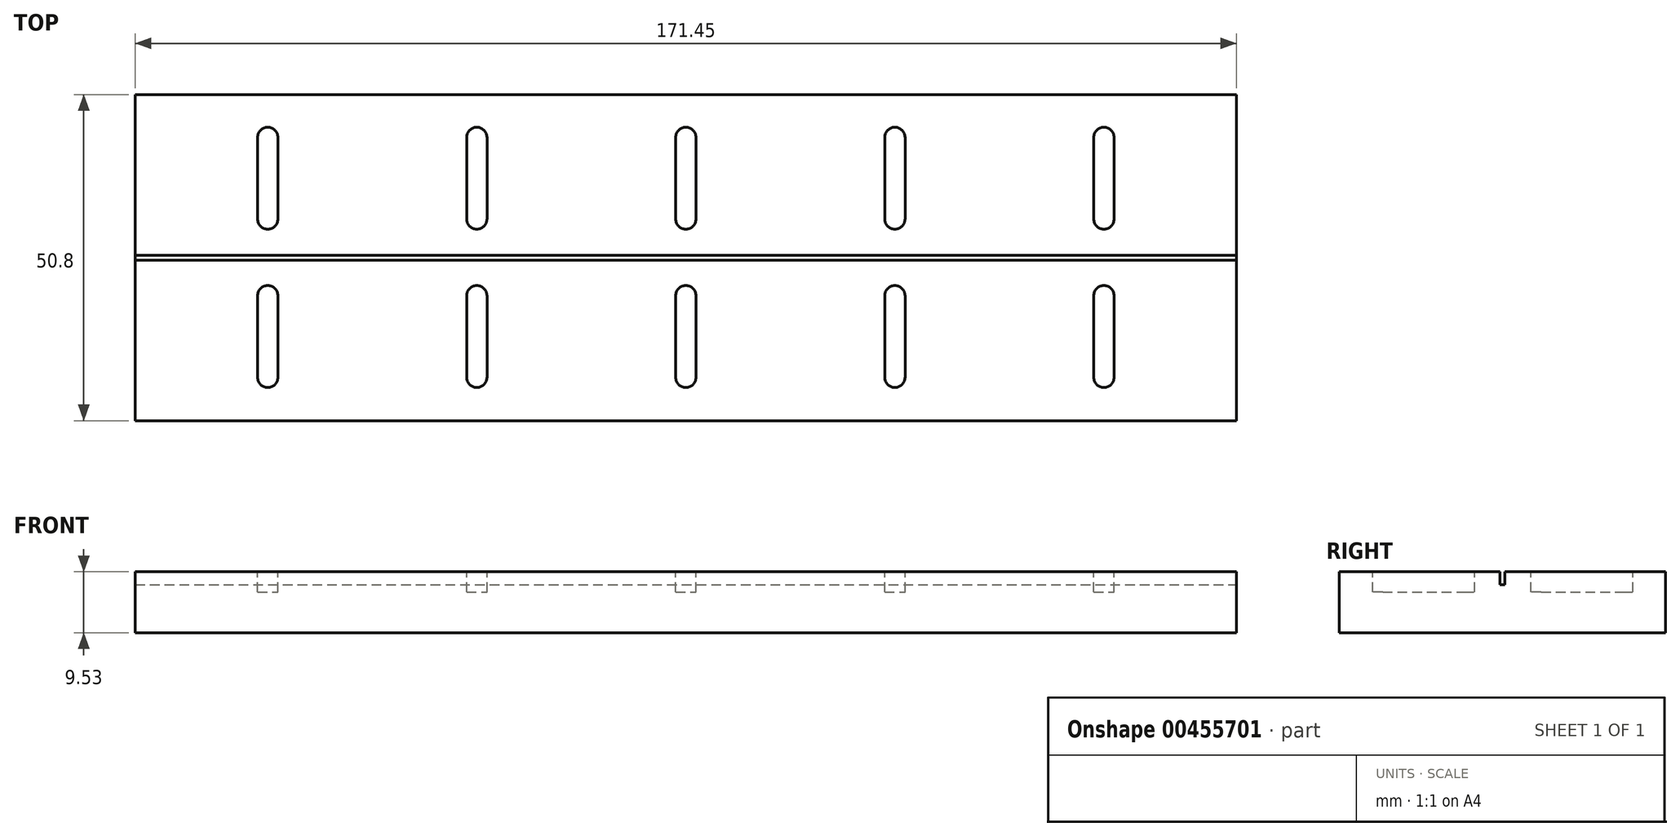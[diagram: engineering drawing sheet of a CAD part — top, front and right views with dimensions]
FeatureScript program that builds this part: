
annotation { "Feature Type Name" : "Feature", "Feature Type Description" : "" }
export const myFeature = defineFeature(function(context is Context, id is Id, definition is map)
    precondition{}
    {
        {
            var Q0;
            Q0=qCreatedBy(makeId("Top.planeOp"),FACE);
            var sketch = newSketch(context, id + "F0", { "sketchPlane" : qUnion([Q0])});
            skLineSegment(sketch, "E0.bottom", {"start": v(112.18, 25.34) * mm, "end": v(-40.22, 25.34) * mm});
            skLineSegment(sketch, "E0.top", {"start": v(112.18, -25.46) * mm, "end": v(-40.22, -25.46) * mm});
            skLineSegment(sketch, "E0.left", {"start": v(112.18, 25.34) * mm, "end": v(112.18, -25.46) * mm});
            skLineSegment(sketch, "E0.right", {"start": v(-40.22, 25.34) * mm, "end": v(-40.22, -25.46) * mm});
            skPoint(sketch, "E0.middle", {"position": v(35.98, -0.06) * mm});
            skLineSegment(sketch, "E1.bottom", {"start": v(-40.22, 0.32) * mm, "end": v(112.18, 0.32) * mm});
            skLineSegment(sketch, "E1.top", {"start": v(-40.22, -0.44) * mm, "end": v(112.18, -0.44) * mm});
            skLineSegment(sketch, "E1.left", {"start": v(-40.22, 0.32) * mm, "end": v(-40.22, -0.44) * mm});
            skLineSegment(sketch, "E1.right", {"start": v(112.18, 0.32) * mm, "end": v(112.18, -0.44) * mm});
            skSolve(sketch);
        }
        {
            var Q0;
            {var subQ0=sQuery(id+"F0.wireOp",EDGE,"E0.top");Q0=makeQuery(id+"F0.imprint","IMPRINT",FACE,{"disambiguationData":[TD([[makeQuery(id+"F0.imprint","IMPRINT",EDGE,{"derivedFrom":subQ0}),-1.0]])]});}
            var Q1;
            {var subQ0=sQuery(id+"F0.wireOp",EDGE,"E0.bottom");Q1=makeQuery(id+"F0.imprint","IMPRINT",FACE,{"disambiguationData":[TD([[makeQuery(id+"F0.imprint","IMPRINT",EDGE,{"derivedFrom":subQ0}),1.0]])]});}
            var Q2;
            Q2=makeQuery(id+"F0.imprint","IMPRINT",FACE,{"disambiguationData":[TD([[makeQuery(id+"F0.imprint","IMPRINT",EDGE,{"derivedFrom":sQuery(id+"F0.wireOp",EDGE,"E1.bottom")}),-1.0]])]});
            extrude(context, id + "F1", {"entities" : qUnion([Q0, Q1, Q2]), "oppositeDirection" : true, "depth" : 9.52 * mm});
        }
        {
            var Q0;
            Q0=makeQuery(id+"F0.imprint","IMPRINT",FACE,{"disambiguationData":[TD([[makeQuery(id+"F0.imprint","IMPRINT",EDGE,{"derivedFrom":sQuery(id+"F0.wireOp",EDGE,"E1.bottom")}),-1.0]])]});
            extrude(context, id + "F2", {"entities" : qUnion([Q0]), "operationType" : NewBodyOperationType.REMOVE, "oppositeDirection" : true, "depth" : 2.03 * mm});
        }
        {
            var Q0;
            {var subQ0=sQuery(id+"F0.wireOp",EDGE,"E0.bottom");var subQ1=sQuery(id+"F0.wireOp",EDGE,"E1.left");var subQ2=sQuery(id+"F0.wireOp",EDGE,"E0.right");var subQ3=sQuery(id+"F0.wireOp",EDGE,"E1.right");var subQ4=sQuery(id+"F0.wireOp",EDGE,"E0.left");Q0=makeQuery(id+"F2.boolean.opBoolean","SPLIT",FACE,{"disambiguationData":[TD([makeQuery(id+"F1.opExtrude","SWEPT_FACE",FACE,{"disambiguationData":[OSD([subQ0])]})])],"derivedFrom":makeQuery(id+"F1.opExtrude","CAP_FACE",FACE,{"disambiguationData":[OSD([subQ0,sQuery(id+"F0.wireOp",EDGE,"E0.top"),subQ4,subQ2,subQ1,subQ3])],"isStart":true})});}
            var sketch = newSketch(context, id + "F3", { "sketchPlane" : qUnion([Q0])});
            skLineSegment(sketch, "E2.left", {"start": v(-30.7, 5.97) * mm, "end": v(-30.7, 18.67) * mm});
            skLineSegment(sketch, "E2.right", {"start": v(-27.52, 5.97) * mm, "end": v(-27.52, 18.67) * mm});
            skArc(sketch, "E3", {"start": v(-27.52, 18.67) * mm, "mid": v(-29.11, 20.26) * mm, "end": v(-30.7, 18.67) * mm});
            skArc(sketch, "E4", {"start": v(-30.7, 5.97) * mm, "mid": v(-29.11, 4.38) * mm, "end": v(-27.52, 5.97) * mm});
            skArc(sketch, "E5.0.1.0", {"start": v(-30.7, -18.7) * mm, "mid": v(-29.11, -20.28) * mm, "end": v(-27.52, -18.7) * mm});
            skArc(sketch, "E5.0.1.1", {"start": v(-27.52, -6) * mm, "mid": v(-29.11, -4.4) * mm, "end": v(-30.7, -6) * mm});
            skLineSegment(sketch, "E5.0.1.2", {"start": v(-27.52, -18.7) * mm, "end": v(-27.52, -6) * mm});
            skLineSegment(sketch, "E5.0.1.3", {"start": v(-30.7, -18.7) * mm, "end": v(-30.7, -6) * mm});
            skArc(sketch, "E5.1.0.0", {"start": v(1.84, 5.97) * mm, "mid": v(3.43, 4.38) * mm, "end": v(5.02, 5.97) * mm});
            skArc(sketch, "E5.1.0.1", {"start": v(5.02, 18.67) * mm, "mid": v(3.43, 20.26) * mm, "end": v(1.84, 18.67) * mm});
            skLineSegment(sketch, "E5.1.0.2", {"start": v(5.02, 5.97) * mm, "end": v(5.02, 18.67) * mm});
            skLineSegment(sketch, "E5.1.0.3", {"start": v(1.84, 5.97) * mm, "end": v(1.84, 18.67) * mm});
            skArc(sketch, "E5.1.1.0", {"start": v(1.84, -18.7) * mm, "mid": v(3.43, -20.28) * mm, "end": v(5.02, -18.7) * mm});
            skArc(sketch, "E5.1.1.1", {"start": v(5.02, -6) * mm, "mid": v(3.43, -4.4) * mm, "end": v(1.84, -6) * mm});
            skLineSegment(sketch, "E5.1.1.2", {"start": v(5.02, -18.7) * mm, "end": v(5.02, -6) * mm});
            skLineSegment(sketch, "E5.1.1.3", {"start": v(1.84, -18.7) * mm, "end": v(1.84, -6) * mm});
            skArc(sketch, "E5.2.0.0", {"start": v(34.39, 5.97) * mm, "mid": v(35.98, 4.38) * mm, "end": v(37.56, 5.97) * mm});
            skArc(sketch, "E5.2.0.1", {"start": v(37.56, 18.67) * mm, "mid": v(35.98, 20.26) * mm, "end": v(34.39, 18.67) * mm});
            skLineSegment(sketch, "E5.2.0.2", {"start": v(37.56, 5.97) * mm, "end": v(37.56, 18.67) * mm});
            skLineSegment(sketch, "E5.2.0.3", {"start": v(34.39, 5.97) * mm, "end": v(34.39, 18.67) * mm});
            skArc(sketch, "E5.2.1.0", {"start": v(34.39, -18.7) * mm, "mid": v(35.98, -20.28) * mm, "end": v(37.56, -18.7) * mm});
            skArc(sketch, "E5.2.1.1", {"start": v(37.56, -6) * mm, "mid": v(35.98, -4.4) * mm, "end": v(34.39, -6) * mm});
            skLineSegment(sketch, "E5.2.1.2", {"start": v(37.56, -18.7) * mm, "end": v(37.56, -6) * mm});
            skLineSegment(sketch, "E5.2.1.3", {"start": v(34.39, -18.7) * mm, "end": v(34.39, -6) * mm});
            skArc(sketch, "E5.3.0.0", {"start": v(66.93, 5.97) * mm, "mid": v(68.52, 4.38) * mm, "end": v(70.1, 5.97) * mm});
            skArc(sketch, "E5.3.0.1", {"start": v(70.1, 18.67) * mm, "mid": v(68.52, 20.26) * mm, "end": v(66.93, 18.67) * mm});
            skLineSegment(sketch, "E5.3.0.2", {"start": v(70.1, 5.97) * mm, "end": v(70.1, 18.67) * mm});
            skLineSegment(sketch, "E5.3.0.3", {"start": v(66.93, 5.97) * mm, "end": v(66.93, 18.67) * mm});
            skArc(sketch, "E5.3.1.0", {"start": v(66.93, -18.7) * mm, "mid": v(68.52, -20.28) * mm, "end": v(70.1, -18.7) * mm});
            skArc(sketch, "E5.3.1.1", {"start": v(70.1, -6) * mm, "mid": v(68.52, -4.4) * mm, "end": v(66.93, -6) * mm});
            skLineSegment(sketch, "E5.3.1.2", {"start": v(70.1, -18.7) * mm, "end": v(70.1, -6) * mm});
            skLineSegment(sketch, "E5.3.1.3", {"start": v(66.93, -18.7) * mm, "end": v(66.93, -6) * mm});
            skArc(sketch, "E5.4.0.0", {"start": v(99.48, 5.97) * mm, "mid": v(101.06, 4.38) * mm, "end": v(102.65, 5.97) * mm});
            skArc(sketch, "E5.4.0.1", {"start": v(102.65, 18.67) * mm, "mid": v(101.06, 20.26) * mm, "end": v(99.48, 18.67) * mm});
            skLineSegment(sketch, "E5.4.0.2", {"start": v(102.65, 5.97) * mm, "end": v(102.65, 18.67) * mm});
            skLineSegment(sketch, "E5.4.0.3", {"start": v(99.48, 5.97) * mm, "end": v(99.48, 18.67) * mm});
            skArc(sketch, "E5.4.1.0", {"start": v(99.48, -18.7) * mm, "mid": v(101.06, -20.28) * mm, "end": v(102.65, -18.7) * mm});
            skArc(sketch, "E5.4.1.1", {"start": v(102.65, -6) * mm, "mid": v(101.06, -4.4) * mm, "end": v(99.48, -6) * mm});
            skLineSegment(sketch, "E5.4.1.2", {"start": v(102.65, -18.7) * mm, "end": v(102.65, -6) * mm});
            skLineSegment(sketch, "E5.4.1.3", {"start": v(99.48, -18.7) * mm, "end": v(99.48, -6) * mm});
            skLineSegment(sketch, "E5.direction1", {"start": v(-30.7, 5.97) * mm, "end": v(1.84, 5.97) * mm, "construction": true});
            skLineSegment(sketch, "E5.direction2", {"start": v(-30.7, 5.97) * mm, "end": v(-30.7, -18.7) * mm, "construction": true});
            skSolve(sketch);
        }
        {
            var Q0;
            Q0=makeQuery(id+"F3.imprint","IMPRINT",FACE,{"disambiguationData":[TD([[makeQuery(id+"F3.imprint","IMPRINT",EDGE,{"derivedFrom":sQuery(id+"F3.wireOp",EDGE,"E2.left")}),-1.0]])]});
            var Q1;
            Q1=makeQuery(id+"F3.imprint","IMPRINT",FACE,{"disambiguationData":[TD([[makeQuery(id+"F3.imprint","IMPRINT",EDGE,{"derivedFrom":sQuery(id+"F3.wireOp",EDGE,"E5.4.1.0")}),1.0]])]});
            var Q2;
            Q2=makeQuery(id+"F3.imprint","IMPRINT",FACE,{"disambiguationData":[TD([[makeQuery(id+"F3.imprint","IMPRINT",EDGE,{"derivedFrom":sQuery(id+"F3.wireOp",EDGE,"E5.0.1.0")}),1.0]])]});
            var Q3;
            Q3=makeQuery(id+"F3.imprint","IMPRINT",FACE,{"disambiguationData":[TD([[makeQuery(id+"F3.imprint","IMPRINT",EDGE,{"derivedFrom":sQuery(id+"F3.wireOp",EDGE,"E5.1.1.0")}),1.0]])]});
            var Q4;
            Q4=makeQuery(id+"F3.imprint","IMPRINT",FACE,{"disambiguationData":[TD([[makeQuery(id+"F3.imprint","IMPRINT",EDGE,{"derivedFrom":sQuery(id+"F3.wireOp",EDGE,"E5.2.1.0")}),1.0]])]});
            var Q5;
            Q5=makeQuery(id+"F3.imprint","IMPRINT",FACE,{"disambiguationData":[TD([[makeQuery(id+"F3.imprint","IMPRINT",EDGE,{"derivedFrom":sQuery(id+"F3.wireOp",EDGE,"E5.3.1.0")}),1.0]])]});
            var Q6;
            Q6=makeQuery(id+"F3.imprint","IMPRINT",FACE,{"disambiguationData":[TD([[makeQuery(id+"F3.imprint","IMPRINT",EDGE,{"derivedFrom":sQuery(id+"F3.wireOp",EDGE,"E5.1.0.0")}),1.0]])]});
            var Q7;
            Q7=makeQuery(id+"F3.imprint","IMPRINT",FACE,{"disambiguationData":[TD([[makeQuery(id+"F3.imprint","IMPRINT",EDGE,{"derivedFrom":sQuery(id+"F3.wireOp",EDGE,"E5.2.0.0")}),1.0]])]});
            var Q8;
            Q8=makeQuery(id+"F3.imprint","IMPRINT",FACE,{"disambiguationData":[TD([[makeQuery(id+"F3.imprint","IMPRINT",EDGE,{"derivedFrom":sQuery(id+"F3.wireOp",EDGE,"E5.3.0.0")}),1.0]])]});
            var Q9;
            Q9=makeQuery(id+"F3.imprint","IMPRINT",FACE,{"disambiguationData":[TD([[makeQuery(id+"F3.imprint","IMPRINT",EDGE,{"derivedFrom":sQuery(id+"F3.wireOp",EDGE,"E5.4.0.0")}),1.0]])]});
            extrude(context, id + "F4", {"entities" : qUnion([Q0, Q1, Q2, Q3, Q4, Q5, Q6, Q7, Q8, Q9]), "operationType" : NewBodyOperationType.REMOVE, "oppositeDirection" : true, "depth" : 3.17 * mm});
        }
        {
            var Q0;
            Q0=makeQuery(id+"F1.opExtrude","SWEPT_FACE",FACE,{"disambiguationData":[OSD([sQuery(id+"F0.wireOp",EDGE,"E0.left"),sQuery(id+"F0.wireOp",EDGE,"E1.right")])]});
            extrude(context, id + "F5", {"entities" : qUnion([Q0]), "operationType" : NewBodyOperationType.ADD, "depth" : 9.52 * mm});
        }
        {
            var Q0;
            Q0=makeQuery(id+"F1.opExtrude","SWEPT_FACE",FACE,{"disambiguationData":[OSD([sQuery(id+"F0.wireOp",EDGE,"E0.right"),sQuery(id+"F0.wireOp",EDGE,"E1.left")])]});
            extrude(context, id + "F6", {"entities" : qUnion([Q0]), "operationType" : NewBodyOperationType.ADD, "depth" : 9.52 * mm});
        }
    });
